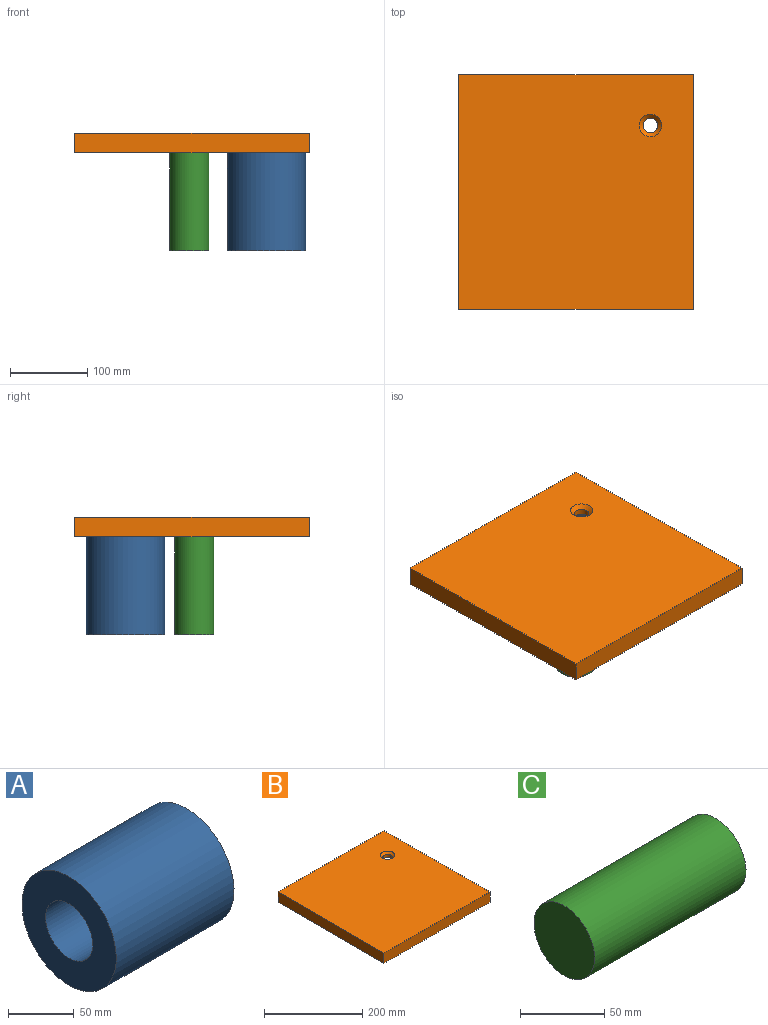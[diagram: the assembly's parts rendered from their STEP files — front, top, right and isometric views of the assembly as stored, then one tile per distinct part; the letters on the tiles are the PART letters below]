
ASSEMBLY  parts=3 mates=2
PART A: 4 faces, bbox 127x101.6x101.6 mm
  f0: cylinder r=25.4mm len=127mm, axis (-1,0,0), area 20268.3mm2, adj f2,f3
  f1: cylinder r=50.8mm len=127mm, axis (-1,0,0), area 40536.6mm2, adj f2,f3
  f2: plane 101.6x101.6mm, normal (1,0,0), area 6080.5mm2, adj f0,f1
  f3: plane 101.6x101.6mm, normal (-1,0,0), area 6080.5mm2, adj f0,f1
PART B: 9 faces, bbox 304.8x304.8x25.4 mm
  f0: plane 304.8x25.4mm, normal (0,-1,0), area 7741.9mm2, adj f1,f3,f4,f5
  f1: plane 304.8x25.4mm, normal (1,0,0), area 7741.9mm2, adj f0,f2,f4,f5
  f2: plane 304.8x25.4mm, normal (0,1,0), area 7741.9mm2, adj f1,f3,f4,f5
  f3: plane 304.8x25.4mm, normal (-1,0,0), area 7741.9mm2, adj f0,f2,f4,f5
  f4: plane 304.8x304.8mm, normal (0,0,1), area 92232.9mm2, adj f0,f1,f2,f3,f7
  f5: plane 304.8x304.8mm, normal (0,0,-1), area 89781.4mm2, adj f0,f1,f2,f3,f8
  f6: cylinder r=9.53mm len=19.05mm, axis (0,0,-1), area 456mm2, adj f7,f8
  f7: cone r=14.61mm half-angle=45deg, axis (0,0,1), area 544.6mm2, adj f4,f6
  f8: cone r=9.53mm half-angle=60deg, axis (0,0,-1), area 3275.4mm2, adj f5,f6
PART C: 3 faces, bbox 127x50.8x50.8 mm
  f0: cylinder r=25.4mm len=127mm, axis (-1,0,0), area 20268.3mm2, adj f1,f2
  f1: plane 50.8x50.8mm, normal (1,0,0), area 2026.8mm2, adj f0
  f2: plane 50.8x50.8mm, normal (-1,0,0), area 2026.8mm2, adj f0
PLACE A rot(axis=(0.71,0,-0.71),180deg) t=(43.44,106.4,-39.82)mm
PLACE B t=(-53.3,20.07,-39.82)mm fixed
PLACE C rot(axis=(-0.58,-0.58,-0.58),120deg) t=(-56.66,17.07,-166.82)mm
MATE fastened A.f0 <-> B.f6  axis (0,0,1) through (43.44,106.4,-39.82)mm
MATE fastened C.f0 <-> B.f5  axis (0,0,1) through (-56.66,17.07,-39.82)mm
